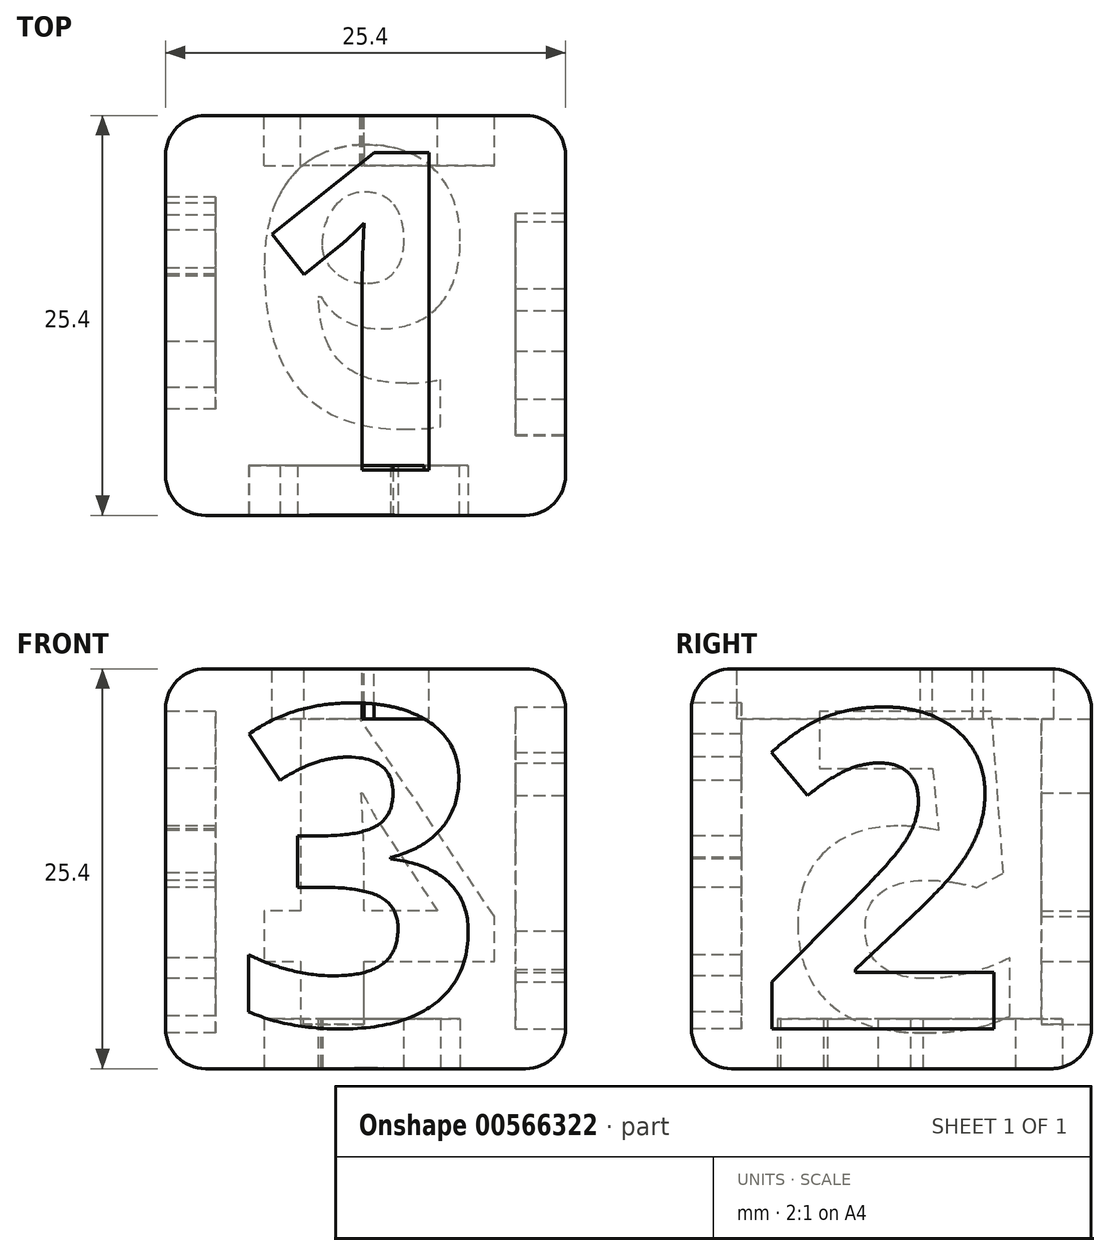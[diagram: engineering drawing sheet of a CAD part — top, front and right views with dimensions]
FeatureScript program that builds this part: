
annotation { "Feature Type Name" : "Feature", "Feature Type Description" : "" }
export const myFeature = defineFeature(function(context is Context, id is Id, definition is map)
    precondition{}
    {
        {
            var Q0;
            Q0=qCreatedBy(makeId("Front.planeOp"),FACE);
            var sketch = newSketch(context, id + "F0", { "sketchPlane" : qUnion([Q0])});
            skLineSegment(sketch, "E0.bottom", {"start": v(0, 0) * mm, "end": v(25.4, 0) * mm});
            skLineSegment(sketch, "E0.top", {"start": v(0, 25.4) * mm, "end": v(25.4, 25.4) * mm});
            skLineSegment(sketch, "E0.left", {"start": v(0, 0) * mm, "end": v(0, 25.4) * mm});
            skLineSegment(sketch, "E0.right", {"start": v(25.4, 0) * mm, "end": v(25.4, 25.4) * mm});
            skSolve(sketch);
        }
        {
            var Q0;
            Q0 = qSketchRegion(id + "F0", true);
            extrude(context, id + "F1", {"entities" : qUnion([Q0]), "depth" : 25.4 * mm, "offsetDistance" : 25.4 * mm});
        }
        {
            var Q0;
            Q0=makeQuery(id+"F1.opExtrude","SWEPT_FACE",FACE,{"disambiguationData":[OSD([sQuery(id+"F0.wireOp",EDGE,"E0.top")])]});
            var sketch = newSketch(context, id + "F2", { "sketchPlane" : qUnion([Q0])});
            skText(sketch, "E1", { "text": "1", "fontName": "OpenSans-Bold.ttf"});
            const initialGuessF2  = {"E1": [0.00508, -0.02252, 1, 0, 0.02032]};
            skSetInitialGuess(sketch, initialGuessF2);
            skSolve(sketch);
        }
        {
            var Q0;
            Q0 = qSketchRegion(id + "F2", true);
            extrude(context, id + "F3", {"entities" : qUnion([Q0]), "operationType" : NewBodyOperationType.REMOVE, "oppositeDirection" : true, "depth" : 3.17 * mm, "offsetDistance" : 25.4 * mm});
        }
        {
            var Q0;
            Q0=makeQuery(id+"F1.opExtrude","SWEPT_FACE",FACE,{"disambiguationData":[OSD([sQuery(id+"F0.wireOp",EDGE,"E0.right")])]});
            var sketch = newSketch(context, id + "F4", { "sketchPlane" : qUnion([Q0])});
            skText(sketch, "E2", { "text": "2", "fontName": "OpenSans-Bold.ttf"});
            const initialGuessF4  = {"E2": [-0.02141, 0.00254, 1, 0, 0.02032]};
            skSetInitialGuess(sketch, initialGuessF4);
            skSolve(sketch);
        }
        {
            var Q0;
            Q0 = qSketchRegion(id + "F4", true);
            extrude(context, id + "F5", {"entities" : qUnion([Q0]), "operationType" : NewBodyOperationType.REMOVE, "oppositeDirection" : true, "depth" : 3.17 * mm, "offsetDistance" : 25.4 * mm});
        }
        {
            var Q0;
            Q0=makeQuery(id+"F1.opExtrude","CAP_FACE",FACE,{"disambiguationData":[OSD([sQuery(id+"F0.wireOp",EDGE,"E0.bottom"),sQuery(id+"F0.wireOp",EDGE,"E0.top"),sQuery(id+"F0.wireOp",EDGE,"E0.left"),sQuery(id+"F0.wireOp",EDGE,"E0.right")])],"isStart":false});
            var sketch = newSketch(context, id + "F6", { "sketchPlane" : qUnion([Q0])});
            skText(sketch, "E3", { "text": "3", "fontName": "OpenSans-Bold.ttf"});
            const initialGuessF6  = {"E3": [0.0042, 0.0028, 1, 0, 0.02032]};
            skSetInitialGuess(sketch, initialGuessF6);
            skSolve(sketch);
        }
        {
            var Q0;
            Q0 = qSketchRegion(id + "F6", true);
            extrude(context, id + "F7", {"entities" : qUnion([Q0]), "operationType" : NewBodyOperationType.REMOVE, "oppositeDirection" : true, "depth" : 3.17 * mm, "offsetDistance" : 25.4 * mm});
        }
        {
            var Q0;
            Q0=makeQuery(id+"F1.opExtrude","CAP_FACE",FACE,{"disambiguationData":[OSD([sQuery(id+"F0.wireOp",EDGE,"E0.bottom"),sQuery(id+"F0.wireOp",EDGE,"E0.top"),sQuery(id+"F0.wireOp",EDGE,"E0.left"),sQuery(id+"F0.wireOp",EDGE,"E0.right")])],"isStart":true});
            var sketch = newSketch(context, id + "F8", { "sketchPlane" : qUnion([Q0])});
            skText(sketch, "E4", { "text": "4", "fontName": "OpenSans-Bold.ttf"});
            const initialGuessF8  = {"E4": [-0.02134, 0.0028, 1, 0, 0.01958]};
            skSetInitialGuess(sketch, initialGuessF8);
            skSolve(sketch);
        }
        {
            var Q0;
            Q0 = qSketchRegion(id + "F8", true);
            extrude(context, id + "F9", {"entities" : qUnion([Q0]), "operationType" : NewBodyOperationType.REMOVE, "oppositeDirection" : true, "depth" : 3.17 * mm, "offsetDistance" : 25.4 * mm});
        }
        {
            var Q0;
            Q0=makeQuery(id+"F1.opExtrude","SWEPT_FACE",FACE,{"disambiguationData":[OSD([sQuery(id+"F0.wireOp",EDGE,"E0.left")])]});
            var sketch = newSketch(context, id + "F10", { "sketchPlane" : qUnion([Q0])});
            skText(sketch, "E5", { "text": "5", "fontName": "OpenSans-Bold.ttf"});
            const initialGuessF10  = {"E5": [0.00381, 0.00254, 1, 0, 0.02032]};
            skSetInitialGuess(sketch, initialGuessF10);
            skSolve(sketch);
        }
        {
            var Q0;
            Q0 = qSketchRegion(id + "F10", true);
            extrude(context, id + "F11", {"entities" : qUnion([Q0]), "operationType" : NewBodyOperationType.REMOVE, "oppositeDirection" : true, "depth" : 3.17 * mm, "offsetDistance" : 25.4 * mm});
        }
        {
            var Q0;
            Q0=makeQuery(id+"F1.opExtrude","SWEPT_FACE",FACE,{"disambiguationData":[OSD([sQuery(id+"F0.wireOp",EDGE,"E0.bottom")])]});
            var sketch = newSketch(context, id + "F12", { "sketchPlane" : qUnion([Q0])});
            skText(sketch, "E6", { "text": "6", "fontName": "OpenSans-Bold.ttf"});
            const initialGuessF12  = {"E6": [0.0054, 0.0021, 1, 0, 0.01778]};
            skSetInitialGuess(sketch, initialGuessF12);
            skSolve(sketch);
        }
        {
            var Q0;
            Q0 = qSketchRegion(id + "F12", true);
            extrude(context, id + "F13", {"entities" : qUnion([Q0]), "operationType" : NewBodyOperationType.REMOVE, "oppositeDirection" : true, "depth" : 3.17 * mm, "offsetDistance" : 25.4 * mm});
        }
        {
            var Q0;
            Q0=makeQuery(id+"F1.opExtrude","SWEPT_EDGE",EDGE,{"disambiguationData":[OSD([sQuery(id+"F0.wireOp",EDGE,"E0.top"),sQuery(id+"F0.wireOp",EDGE,"E0.right")])]});
            fillet(context, id + "F14", {"entities" : qUnion([Q0]), "radius" : 2.54 * mm, "tangentPropagation" : true, "allowEdgeOverflow" : false});
        }
        {
            var Q0;
            Q0=makeQuery(id+"F1.opExtrude","CAP_EDGE",EDGE,{"disambiguationData":[OSD([sQuery(id+"F0.wireOp",EDGE,"E0.right")])],"isStart":false});
            fillet(context, id + "F15", {"entities" : qUnion([Q0]), "radius" : 2.54 * mm, "tangentPropagation" : true, "allowEdgeOverflow" : false});
        }
        {
            var Q0;
            Q0=makeQuery(id+"F1.opExtrude","CAP_EDGE",EDGE,{"disambiguationData":[OSD([sQuery(id+"F0.wireOp",EDGE,"E0.right")])],"isStart":true});
            fillet(context, id + "F16", {"entities" : qUnion([Q0]), "radius" : 2.54 * mm, "tangentPropagation" : true, "allowEdgeOverflow" : false});
        }
        {
            var Q0;
            Q0=makeQuery(id+"F1.opExtrude","CAP_EDGE",EDGE,{"disambiguationData":[OSD([sQuery(id+"F0.wireOp",EDGE,"E0.left")])],"isStart":true});
            fillet(context, id + "F17", {"entities" : qUnion([Q0]), "radius" : 2.54 * mm, "tangentPropagation" : true, "allowEdgeOverflow" : false});
        }
        {
            var Q0;
            Q0=makeQuery(id+"F1.opExtrude","CAP_EDGE",EDGE,{"disambiguationData":[OSD([sQuery(id+"F0.wireOp",EDGE,"E0.bottom")])],"isStart":true});
            fillet(context, id + "F18", {"entities" : qUnion([Q0]), "radius" : 2.54 * mm, "tangentPropagation" : true, "allowEdgeOverflow" : false});
        }
    });
